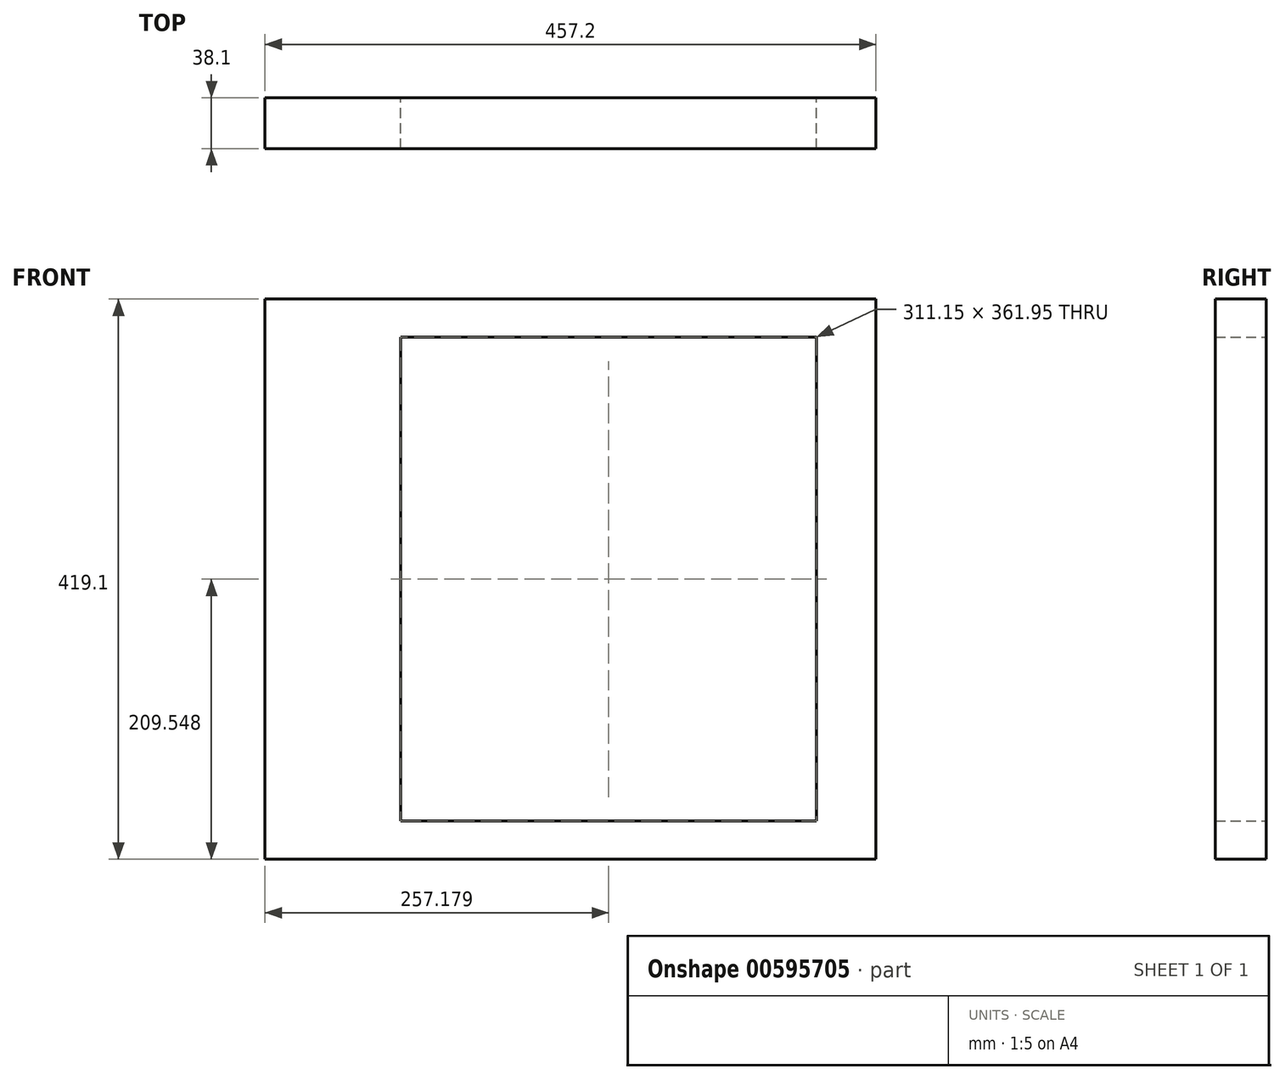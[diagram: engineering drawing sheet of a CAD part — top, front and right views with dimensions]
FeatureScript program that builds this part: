
annotation { "Feature Type Name" : "Feature", "Feature Type Description" : "" }
export const myFeature = defineFeature(function(context is Context, id is Id, definition is map)
    precondition{}
    {
        {
            var Q0;
            Q0=qCreatedBy(makeId("Front.planeOp"),FACE);
            var sketch = newSketch(context, id + "F0", { "sketchPlane" : qUnion([Q0])});
            skLineSegment(sketch, "E0.bottom", {"start": v(-98.08, 192.74) * mm, "end": v(213.07, 192.74) * mm});
            skLineSegment(sketch, "E0.top", {"start": v(-98.08, -169.2) * mm, "end": v(213.07, -169.2) * mm});
            skLineSegment(sketch, "E0.left", {"start": v(-98.08, 192.74) * mm, "end": v(-98.08, -169.2) * mm});
            skLineSegment(sketch, "E0.right", {"start": v(213.07, 192.74) * mm, "end": v(213.07, -169.2) * mm});
            skLineSegment(sketch, "E1.bottom", {"start": v(-199.68, 221.32) * mm, "end": v(257.52, 221.32) * mm});
            skLineSegment(sketch, "E1.top", {"start": v(-199.68, -197.78) * mm, "end": v(257.52, -197.78) * mm});
            skLineSegment(sketch, "E1.left", {"start": v(-199.68, 221.32) * mm, "end": v(-199.68, -197.78) * mm});
            skLineSegment(sketch, "E1.right", {"start": v(257.52, 221.32) * mm, "end": v(257.52, -197.78) * mm});
            skSolve(sketch);
        }
        {
            var Q0;
            Q0 = qSketchRegion(id + "F0", true);
            var Q1;
            Q1=makeQuery(id+"F0.imprint","IMPRINT",FACE,{"disambiguationData":[TD([[makeQuery(id+"F0.imprint","IMPRINT",EDGE,{"derivedFrom":sQuery(id+"F0.wireOp",EDGE,"E0.bottom")}),1.0]])]});
            extrude(context, id + "F1", {"entities" : qUnion([Q0, Q1]), "depth" : 38.1 * mm, "offsetDistance" : 25.4 * mm});
        }
    });
